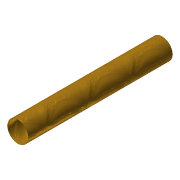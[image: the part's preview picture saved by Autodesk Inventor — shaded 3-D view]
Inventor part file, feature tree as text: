
AUTODESK INVENTOR PART (.ipt)
format: ipt  version: 2014 SP1 (Build 180222100, 222)  size: 77,312 bytes
history: native  units: in
note: dims shown in document units (in); Inventor stores cm internally (conversion verified against a paired STEP export)
features: extrude x1, sketch x1
ambient origin geometry x8: Origin, YZ Plane, XZ Plane, XY Plane, X Axis, Y Axis, Z Axis, Center Point
bodies: Solid1 (feature_tree)
feature tree (2):
  extrude  "Extrusion1"  Depth=5.95in
  sketch  "Sketch1"  dims[d0=0.857in d1=0.866in d2=5.95in d3=0.0in]
